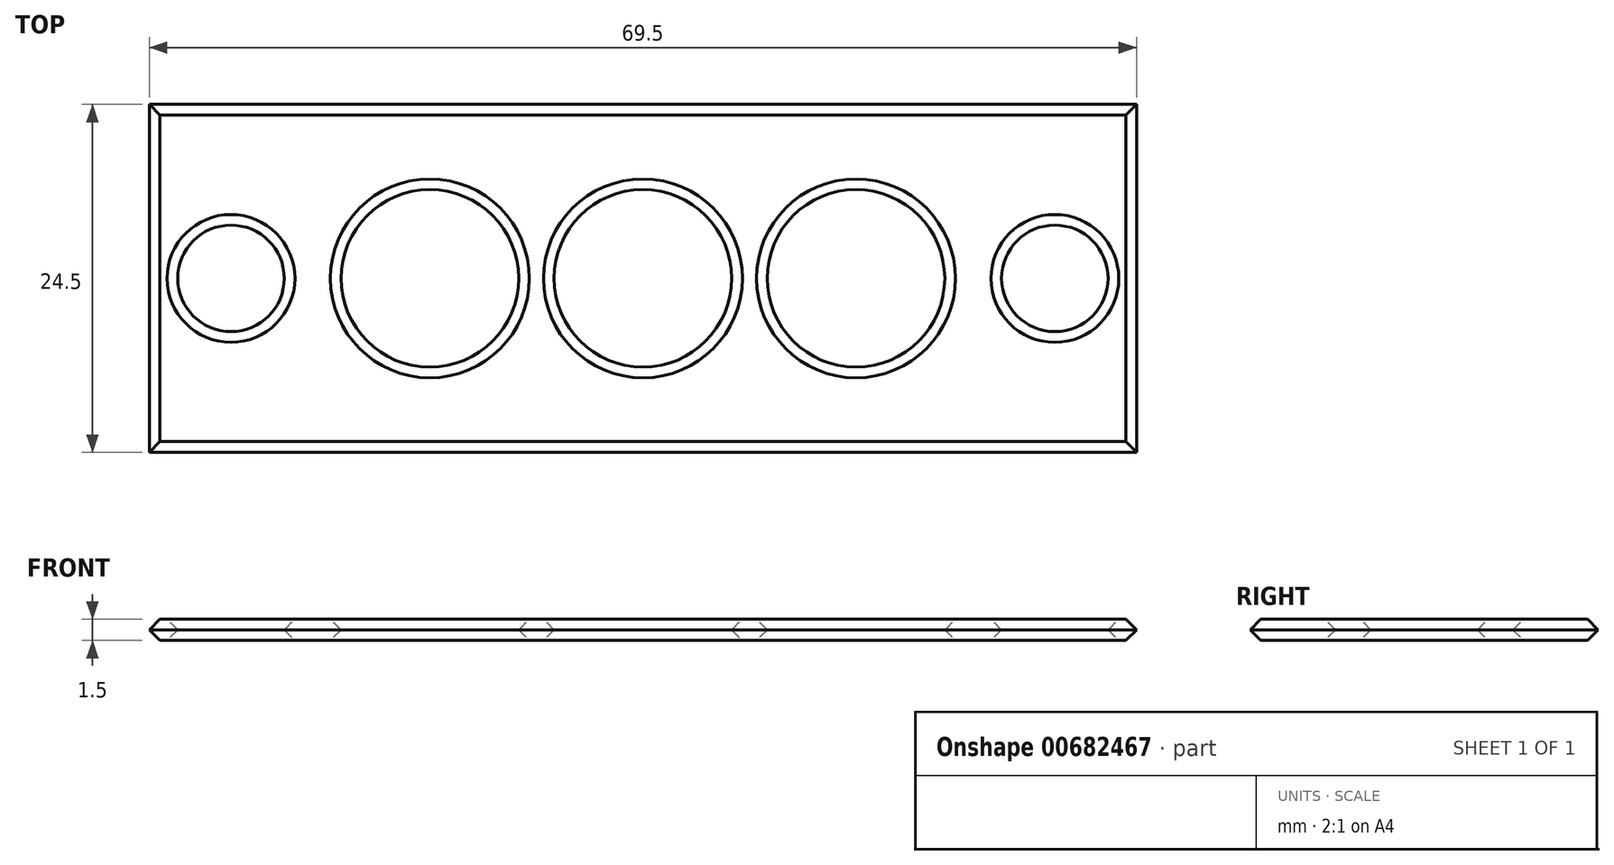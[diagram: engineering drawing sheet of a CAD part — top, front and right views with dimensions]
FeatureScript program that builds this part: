
annotation { "Feature Type Name" : "Feature", "Feature Type Description" : "" }
export const myFeature = defineFeature(function(context is Context, id is Id, definition is map)
    precondition{}
    {
        {
            var Q0;
            Q0=qCreatedBy(makeId("Top.planeOp"),FACE);
            var sketch = newSketch(context, id + "F0", { "sketchPlane" : qUnion([Q0])});
            skLineSegment(sketch, "E0.bottom", {"start": v(35, -12.5) * mm, "end": v(-35, -12.5) * mm});
            skLineSegment(sketch, "E0.top", {"start": v(35, 12.5) * mm, "end": v(-35, 12.5) * mm});
            skLineSegment(sketch, "E0.left", {"start": v(35, -12.5) * mm, "end": v(35, 12.5) * mm});
            skLineSegment(sketch, "E0.right", {"start": v(-35, -12.5) * mm, "end": v(-35, 12.5) * mm});
            skPoint(sketch, "E0.middle", {"position": v(0, 0) * mm});
            skPoint(sketch, "E1", {"position": v(-29, 0) * mm});
            skPoint(sketch, "E2", {"position": v(29, 0) * mm});
            skPoint(sketch, "E3", {"position": v(-15, 0) * mm});
            skPoint(sketch, "E4", {"position": v(15, 0) * mm});
            skSolve(sketch);
        }
        {
            var Q0;
            Q0=makeQuery(id+"F0.imprint","IMPRINT",FACE,{"disambiguationData":[TD([[makeQuery(id+"F0.imprint","IMPRINT",EDGE,{"derivedFrom":sQuery(id+"F0.wireOp",EDGE,"E0.bottom")}),-1.0]])]});
            extrude(context, id + "F1", {"entities" : qUnion([Q0]), "depth" : 1.5 * mm, "offsetDistance" : 25 * mm});
        }
        {
            var Q0;
            Q0=sQuery(id+"F0.wireOp",VERTEX,"E1");
            var Q1;
            Q1=sQuery(id+"F0.wireOp",VERTEX,"E2");
            var Q2;
            Q2=makeQuery(id+"F1.opExtrude","SWEPT_BODY",BODY,{"disambiguationData":[OSD([sQuery(id+"F0.wireOp",EDGE,"E0.bottom"),sQuery(id+"F0.wireOp",EDGE,"E0.top"),sQuery(id+"F0.wireOp",EDGE,"E0.left"),sQuery(id+"F0.wireOp",EDGE,"E0.right")])]});
            hole(context, id + "F2", {"style" : HoleStyle.SIMPLE, "endStyle" : HoleEndStyle.THROUGH, "oppositeDirection" : true, "holeDiameter" : 7 * mm, "majorDiameter" : 5 * mm, "isTappedThrough" : true, "tappedDepth" : 12 * mm, "tapClearance" : 3, "startFromSketch" : true, "locations" : qUnion([Q0, Q1]), "scope" : qUnion([Q2])});
        }
        {
            var Q0;
            Q0=sQuery(id+"F0.wireOp",VERTEX,"E3");
            var Q1;
            Q1=sQuery(id+"F0.wireOp",VERTEX,"E0.middle");
            var Q2;
            Q2=sQuery(id+"F0.wireOp",VERTEX,"E4");
            var Q3;
            Q3=makeQuery(id+"F1.opExtrude","SWEPT_BODY",BODY,{"disambiguationData":[OSD([sQuery(id+"F0.wireOp",EDGE,"E0.bottom"),sQuery(id+"F0.wireOp",EDGE,"E0.top"),sQuery(id+"F0.wireOp",EDGE,"E0.left"),sQuery(id+"F0.wireOp",EDGE,"E0.right")])]});
            hole(context, id + "F3", {"style" : HoleStyle.SIMPLE, "endStyle" : HoleEndStyle.THROUGH, "oppositeDirection" : true, "holeDiameter" : 12 * mm, "majorDiameter" : 5 * mm, "isTappedThrough" : true, "tappedDepth" : 12 * mm, "tapClearance" : 3, "startFromSketch" : true, "locations" : qUnion([Q0, Q1, Q2]), "scope" : qUnion([Q3])});
        }
        {
            var Q0;
            Q0=makeQuery(id+"F1.opExtrude","CAP_FACE",FACE,{"disambiguationData":[OSD([sQuery(id+"F0.wireOp",EDGE,"E0.bottom"),sQuery(id+"F0.wireOp",EDGE,"E0.top"),sQuery(id+"F0.wireOp",EDGE,"E0.left"),sQuery(id+"F0.wireOp",EDGE,"E0.right")])],"isStart":false});
            chamfer(context, id + "F4", {"entities" : qUnion([Q0]), "width" : 1 * mm, "tangentPropagation" : true});
        }
        {
            var Q0;
            Q0=makeQuery(id+"F1.opExtrude","CAP_FACE",FACE,{"disambiguationData":[OSD([sQuery(id+"F0.wireOp",EDGE,"E0.bottom"),sQuery(id+"F0.wireOp",EDGE,"E0.top"),sQuery(id+"F0.wireOp",EDGE,"E0.left"),sQuery(id+"F0.wireOp",EDGE,"E0.right")])],"isStart":true});
            chamfer(context, id + "F5", {"entities" : qUnion([Q0]), "width" : 1 * mm, "tangentPropagation" : true});
        }
    });
